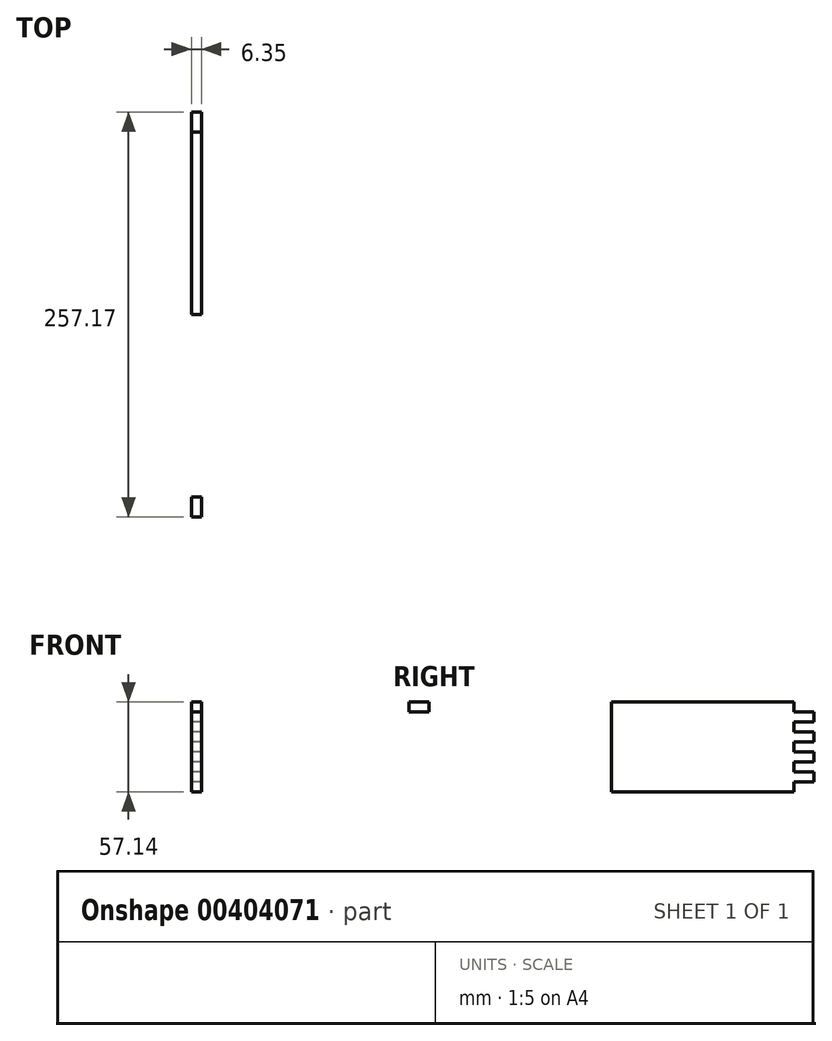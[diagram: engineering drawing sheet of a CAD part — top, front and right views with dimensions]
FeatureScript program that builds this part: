
annotation { "Feature Type Name" : "Feature", "Feature Type Description" : "" }
export const myFeature = defineFeature(function(context is Context, id is Id, definition is map)
    precondition{}
    {
        {
            var Q0;
            Q0=qCreatedBy(makeId("Right.planeOp"),FACE);
            var sketch = newSketch(context, id + "F0", { "sketchPlane" : qUnion([Q0])});
            skLineSegment(sketch, "E0.bottom", {"start": v(-64.3, 28.57) * mm, "end": v(64.3, 28.57) * mm});
            skLineSegment(sketch, "E0.top", {"start": v(-64.3, -28.58) * mm, "end": v(64.3, -28.58) * mm});
            skLineSegment(sketch, "E0.left", {"start": v(-64.3, 28.58) * mm, "end": v(-64.3, -28.58) * mm});
            skLineSegment(sketch, "E0.right", {"start": v(64.3, 28.58) * mm, "end": v(64.3, -28.58) * mm});
            skPoint(sketch, "E0.middle", {"position": v(0, 0) * mm});
            skLineSegment(sketch, "E1.bottom", {"start": v(-64.3, 28.57) * mm, "end": v(-51.6, 28.57) * mm});
            skLineSegment(sketch, "E1.top", {"start": v(-64.3, 22.23) * mm, "end": v(-51.6, 22.23) * mm});
            skLineSegment(sketch, "E1.left", {"start": v(-64.3, 28.57) * mm, "end": v(-64.3, 22.23) * mm});
            skLineSegment(sketch, "E1.right", {"start": v(-51.6, 28.58) * mm, "end": v(-51.6, 22.23) * mm});
            skLineSegment(sketch, "E2.0.1.0", {"start": v(-64.3, 15.88) * mm, "end": v(-51.6, 15.88) * mm});
            skLineSegment(sketch, "E2.0.1.1", {"start": v(-64.3, 9.53) * mm, "end": v(-51.6, 9.53) * mm});
            skLineSegment(sketch, "E2.0.1.2", {"start": v(-64.3, 15.88) * mm, "end": v(-64.3, 9.53) * mm});
            skLineSegment(sketch, "E2.0.1.3", {"start": v(-51.6, 15.88) * mm, "end": v(-51.6, 9.53) * mm});
            skLineSegment(sketch, "E2.0.2.0", {"start": v(-64.3, 3.17) * mm, "end": v(-51.6, 3.17) * mm});
            skLineSegment(sketch, "E2.0.2.1", {"start": v(-64.3, -3.18) * mm, "end": v(-51.6, -3.18) * mm});
            skLineSegment(sketch, "E2.0.2.2", {"start": v(-64.3, 3.17) * mm, "end": v(-64.3, -3.18) * mm});
            skLineSegment(sketch, "E2.0.2.3", {"start": v(-51.6, 3.18) * mm, "end": v(-51.6, -3.17) * mm});
            skLineSegment(sketch, "E2.0.3.0", {"start": v(-64.3, -9.53) * mm, "end": v(-51.6, -9.53) * mm});
            skLineSegment(sketch, "E2.0.3.1", {"start": v(-64.3, -15.88) * mm, "end": v(-51.6, -15.88) * mm});
            skLineSegment(sketch, "E2.0.3.2", {"start": v(-64.3, -9.53) * mm, "end": v(-64.3, -15.88) * mm});
            skLineSegment(sketch, "E2.0.3.3", {"start": v(-51.6, -9.52) * mm, "end": v(-51.6, -15.87) * mm});
            skLineSegment(sketch, "E2.0.4.0", {"start": v(-64.3, -22.23) * mm, "end": v(-51.6, -22.23) * mm});
            skLineSegment(sketch, "E2.0.4.1", {"start": v(-64.3, -28.58) * mm, "end": v(-51.6, -28.58) * mm});
            skLineSegment(sketch, "E2.0.4.2", {"start": v(-64.3, -22.23) * mm, "end": v(-64.3, -28.58) * mm});
            skLineSegment(sketch, "E2.0.4.3", {"start": v(-51.6, -22.22) * mm, "end": v(-51.6, -28.57) * mm});
            skLineSegment(sketch, "E2.direction1", {"start": v(-64.3, 22.23) * mm, "end": v(-38.9, 22.23) * mm, "construction": true});
            skLineSegment(sketch, "E2.direction2", {"start": v(-64.3, 22.23) * mm, "end": v(-64.3, 9.53) * mm, "construction": true});
            skLineSegment(sketch, "E3.MirrorCS", {"start": v(192.88, 15.87) * mm, "end": v(192.88, 9.52) * mm});
            skLineSegment(sketch, "E4.MirrorCS", {"start": v(192.88, 22.22) * mm, "end": v(180.18, 22.22) * mm});
            skLineSegment(sketch, "E5.MirrorCS", {"start": v(192.88, 3.17) * mm, "end": v(192.88, -3.18) * mm});
            skLineSegment(sketch, "E6.MirrorCS", {"start": v(192.88, -28.58) * mm, "end": v(180.18, -28.58) * mm});
            skLineSegment(sketch, "E7.MirrorCS", {"start": v(192.88, 28.57) * mm, "end": v(180.18, 28.57) * mm});
            skLineSegment(sketch, "E8.MirrorCS", {"start": v(192.88, 22.22) * mm, "end": v(192.88, 9.52) * mm, "construction": true});
            skLineSegment(sketch, "E9.MirrorCS", {"start": v(192.88, 22.22) * mm, "end": v(167.48, 22.22) * mm, "construction": true});
            skLineSegment(sketch, "E10.MirrorCS", {"start": v(192.88, 28.57) * mm, "end": v(64.3, 28.57) * mm});
            skLineSegment(sketch, "E11.MirrorCS", {"start": v(192.88, 28.57) * mm, "end": v(192.88, 22.22) * mm});
            skLineSegment(sketch, "E12.MirrorCS", {"start": v(180.18, -22.23) * mm, "end": v(180.18, -28.58) * mm});
            skLineSegment(sketch, "E13.MirrorCS", {"start": v(192.88, -28.58) * mm, "end": v(64.3, -28.58) * mm});
            skLineSegment(sketch, "E14.MirrorCS", {"start": v(192.88, -9.53) * mm, "end": v(192.88, -15.88) * mm});
            skLineSegment(sketch, "E15.MirrorCS", {"start": v(180.18, 3.17) * mm, "end": v(180.18, -3.18) * mm});
            skLineSegment(sketch, "E16.MirrorCS", {"start": v(192.88, -3.18) * mm, "end": v(180.18, -3.18) * mm});
            skLineSegment(sketch, "E17.MirrorCS", {"start": v(192.88, -22.23) * mm, "end": v(180.18, -22.23) * mm});
            skPoint(sketch, "E18.MirrorP", {"position": v(128.59, 0) * mm});
            skLineSegment(sketch, "E19.MirrorCS", {"start": v(192.88, -15.88) * mm, "end": v(180.18, -15.88) * mm});
            skLineSegment(sketch, "E20.MirrorCS", {"start": v(192.88, 28.57) * mm, "end": v(192.88, -28.58) * mm});
            skLineSegment(sketch, "E21.MirrorCS", {"start": v(180.18, 15.87) * mm, "end": v(180.18, 9.52) * mm});
            skLineSegment(sketch, "E22.MirrorCS", {"start": v(192.88, -9.53) * mm, "end": v(180.18, -9.53) * mm});
            skLineSegment(sketch, "E23.MirrorCS", {"start": v(192.88, -22.23) * mm, "end": v(192.88, -28.58) * mm});
            skLineSegment(sketch, "E24.MirrorCS", {"start": v(180.18, 28.57) * mm, "end": v(180.18, 22.22) * mm});
            skLineSegment(sketch, "E25.MirrorCS", {"start": v(192.88, 15.87) * mm, "end": v(180.18, 15.87) * mm});
            skLineSegment(sketch, "E26.MirrorCS", {"start": v(192.88, 9.52) * mm, "end": v(180.18, 9.52) * mm});
            skLineSegment(sketch, "E27.MirrorCS", {"start": v(180.18, -9.53) * mm, "end": v(180.18, -15.88) * mm});
            skLineSegment(sketch, "E28.MirrorCS", {"start": v(192.88, 3.17) * mm, "end": v(180.18, 3.17) * mm});
            skSolve(sketch);
        }
        {
            var Q0;
            Q0=makeQuery(id+"F0.imprint","IMPRINT",FACE,{"disambiguationData":[TD([[makeQuery(id+"F0.imprint","IMPRINT",EDGE,{"derivedFrom":sQuery(id+"F0.wireOp",EDGE,"E0.bottom")}),-1.0]])]});
            var Q1;
            {var subQ4=sQuery(id+"F0.wireOp",EDGE,"E0.right");Q1=makeQuery(id+"F0.imprint","IMPRINT",FACE,{"disambiguationData":[TD([[makeQuery(id+"F0.imprint","IMPRINT",EDGE,{"derivedFrom":subQ4}),1.0]])]});}
            extrude(context, id + "F1", {"entities" : qUnion([Q0, Q1]), "depth" : 6.35 * mm});
        }
    });
